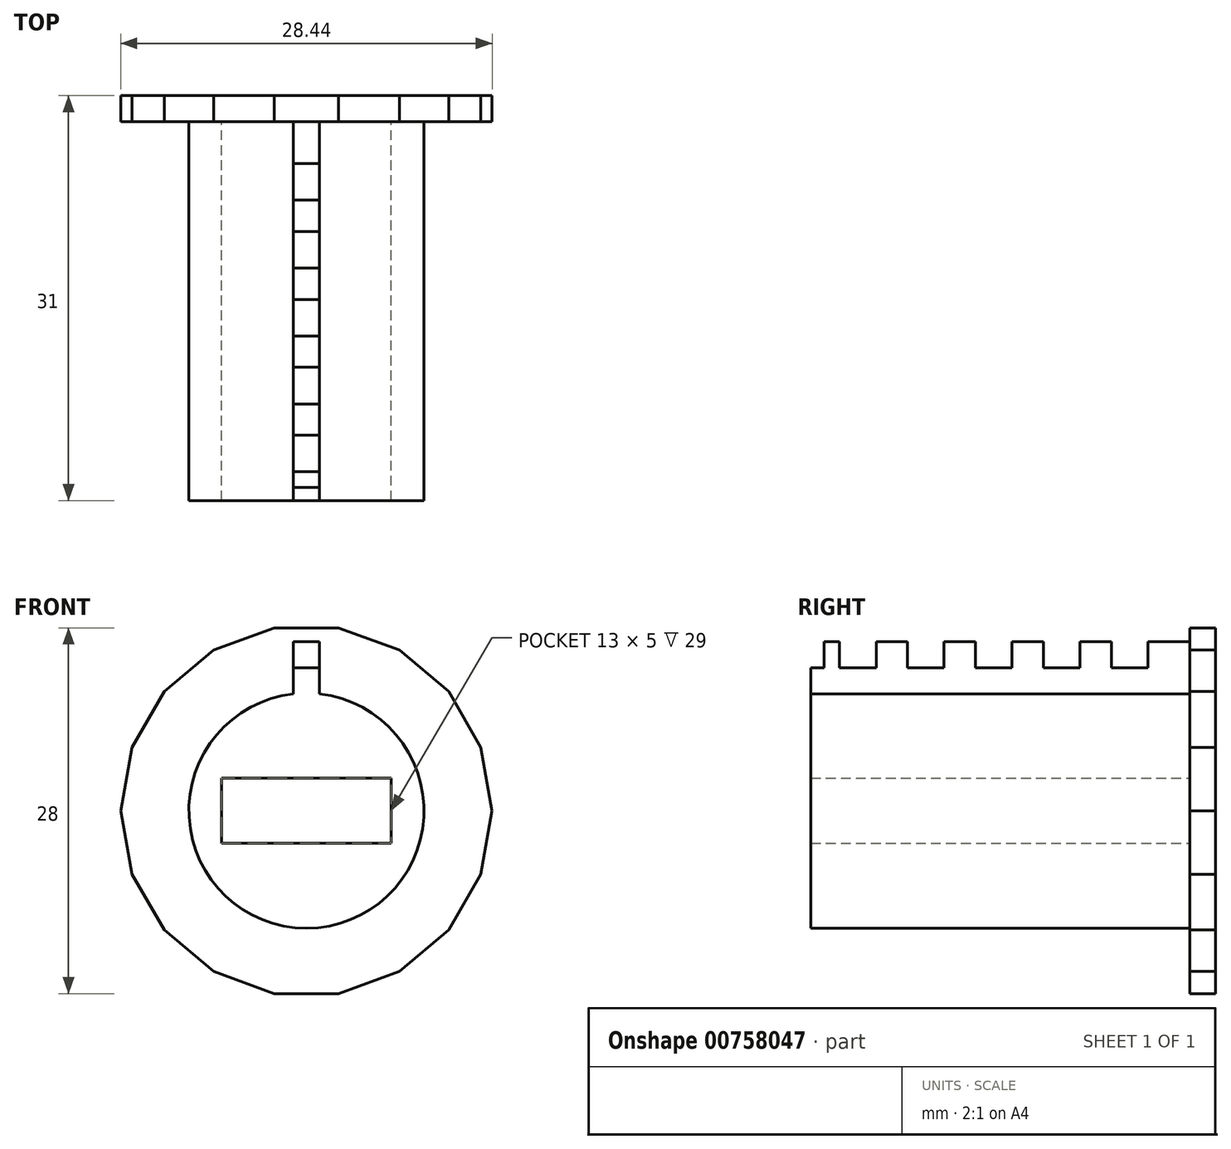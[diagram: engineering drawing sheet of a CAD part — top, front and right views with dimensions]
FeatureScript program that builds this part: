
annotation { "Feature Type Name" : "Feature", "Feature Type Description" : "" }
export const myFeature = defineFeature(function(context is Context, id is Id, definition is map)
    precondition{}
    {
        {
            var Q0;
            Q0=qCreatedBy(makeId("Front.planeOp"),FACE);
            var sketch = newSketch(context, id + "F0", { "sketchPlane" : qUnion([Q0])});
            skCircle(sketch, "E0", {"center": v(0, 0) * mm, "radius": 9 * mm});
            skCircle(sketch, "E1.cCircle", {"center": v(0, 0) * mm, "radius": 14 * mm, "construction": true});
            skLineSegment(sketch, "E1.0", {"start": v(-2.47, 14) * mm, "end": v(2.47, 14) * mm});
            skLineSegment(sketch, "E1.1", {"start": v(2.47, 14) * mm, "end": v(7.1, 12.31) * mm});
            skLineSegment(sketch, "E1.2", {"start": v(7.1, 12.31) * mm, "end": v(10.9, 9.14) * mm});
            skLineSegment(sketch, "E1.3", {"start": v(10.9, 9.14) * mm, "end": v(13.36, 4.86) * mm});
            skLineSegment(sketch, "E1.4", {"start": v(13.36, 4.86) * mm, "end": v(14.22, 0) * mm});
            skLineSegment(sketch, "E1.5", {"start": v(14.22, 0) * mm, "end": v(13.36, -4.86) * mm});
            skLineSegment(sketch, "E1.6", {"start": v(13.36, -4.86) * mm, "end": v(10.9, -9.14) * mm});
            skLineSegment(sketch, "E1.7", {"start": v(10.9, -9.14) * mm, "end": v(7.1, -12.31) * mm});
            skLineSegment(sketch, "E1.8", {"start": v(7.1, -12.31) * mm, "end": v(2.47, -14) * mm});
            skLineSegment(sketch, "E1.9", {"start": v(2.47, -14) * mm, "end": v(-2.47, -14) * mm});
            skLineSegment(sketch, "E1.10", {"start": v(-2.47, -14) * mm, "end": v(-7.1, -12.31) * mm});
            skLineSegment(sketch, "E1.11", {"start": v(-7.1, -12.31) * mm, "end": v(-10.9, -9.14) * mm});
            skLineSegment(sketch, "E1.12", {"start": v(-10.9, -9.14) * mm, "end": v(-13.36, -4.86) * mm});
            skLineSegment(sketch, "E1.13", {"start": v(-13.36, -4.86) * mm, "end": v(-14.22, 0) * mm});
            skLineSegment(sketch, "E1.14", {"start": v(-14.22, 0) * mm, "end": v(-13.36, 4.86) * mm});
            skLineSegment(sketch, "E1.15", {"start": v(-13.36, 4.86) * mm, "end": v(-10.9, 9.14) * mm});
            skLineSegment(sketch, "E1.16", {"start": v(-10.9, 9.14) * mm, "end": v(-7.1, 12.31) * mm});
            skLineSegment(sketch, "E1.17", {"start": v(-7.1, 12.31) * mm, "end": v(-2.47, 14) * mm});
            skPoint(sketch, "E1.0.midPoint", {"position": v(0, 14) * mm});
            skLineSegment(sketch, "E2.top", {"start": v(-1, 10.94) * mm, "end": v(1, 10.94) * mm});
            skLineSegment(sketch, "E2.left", {"start": v(-1, 8.94) * mm, "end": v(-1, 10.94) * mm});
            skLineSegment(sketch, "E2.right", {"start": v(1, 8.94) * mm, "end": v(1, 10.94) * mm});
            skLineSegment(sketch, "E3.bottom", {"start": v(7, 2.5) * mm, "end": v(-7, 2.5) * mm});
            skLineSegment(sketch, "E3.top", {"start": v(7, -2.5) * mm, "end": v(-7, -2.5) * mm});
            skLineSegment(sketch, "E3.left", {"start": v(7, 2.5) * mm, "end": v(7, -2.5) * mm});
            skLineSegment(sketch, "E3.right", {"start": v(-7, 2.5) * mm, "end": v(-7, -2.5) * mm});
            skSolve(sketch);
        }
        {
            var Q0;
            Q0 = qSketchRegion(id + "F0", true);
            var Q1;
            Q1=makeQuery(id+"F0.imprint","IMPRINT",FACE,{"disambiguationData":[TD([[makeQuery(id+"F0.imprint","IMPRINT",EDGE,{"derivedFrom":sQuery(id+"F0.wireOp",EDGE,"E2.top")}),-1.0]])]});
            var Q2;
            Q2=makeQuery(id+"F0.imprint","IMPRINT",FACE,{"disambiguationData":[TD([[makeQuery(id+"F0.imprint","IMPRINT",EDGE,{"derivedFrom":sQuery(id+"F0.wireOp",EDGE,"E3.bottom")}),-1.0]])]});
            var Q3;
            Q3=makeQuery(id+"F0.imprint","IMPRINT",FACE,{"disambiguationData":[TD([[makeQuery(id+"F0.imprint","IMPRINT",EDGE,{"derivedFrom":sQuery(id+"F0.wireOp",EDGE,"E3.bottom")}),1.0]])]});
            extrude(context, id + "F1", {"entities" : qUnion([Q0, Q1, Q2, Q3]), "depth" : 2 * mm, "offsetDistance" : 25 * mm});
        }
        {
            var Q0;
            Q0=qCreatedBy(makeId("Front.planeOp"),FACE);
            var sketch = newSketch(context, id + "F2", { "sketchPlane" : qUnion([Q0])});
            skLineSegment(sketch, "E4.bottom", {"start": v(6.5, 2.5) * mm, "end": v(-6.5, 2.5) * mm});
            skLineSegment(sketch, "E4.top", {"start": v(6.5, -2.5) * mm, "end": v(-6.5, -2.5) * mm});
            skLineSegment(sketch, "E4.left", {"start": v(6.5, 2.5) * mm, "end": v(6.5, -2.5) * mm});
            skLineSegment(sketch, "E4.right", {"start": v(-6.5, 2.5) * mm, "end": v(-6.5, -2.5) * mm});
            skPoint(sketch, "E4.middle", {"position": v(0, 0) * mm});
            skArc(sketch, "E5", {"start": v(-1, 8.94) * mm, "mid": v(0, -9) * mm, "end": v(1, 8.94) * mm});
            skLineSegment(sketch, "E6.top", {"start": v(-1, 10.94) * mm, "end": v(1, 10.94) * mm});
            skLineSegment(sketch, "E6.left", {"start": v(-1, 8.94) * mm, "end": v(-1, 10.94) * mm});
            skLineSegment(sketch, "E6.right", {"start": v(1, 8.94) * mm, "end": v(1, 10.94) * mm});
            skSolve(sketch);
        }
        {
            var Q0;
            Q0 = qSketchRegion(id + "F2", true);
            extrude(context, id + "F3", {"entities" : qUnion([Q0]), "operationType" : NewBodyOperationType.ADD, "depth" : 31 * mm, "offsetDistance" : 25 * mm});
        }
        {
            var Q0;
            Q0=makeQuery(id+"F3.opExtrude","SWEPT_FACE",FACE,{"disambiguationData":[OSD([sQuery(id+"F2.wireOp",EDGE,"E6.top")])]});
            var sketch = newSketch(context, id + "F4", { "sketchPlane" : qUnion([Q0])});
            skLineSegment(sketch, "E7.left", {"start": v(1, -2) * mm, "end": v(1, -4) * mm});
            skLineSegment(sketch, "E7.right", {"start": v(-1, -2) * mm, "end": v(-1, -4) * mm});
            skLineSegment(sketch, "E8.left", {"start": v(1, -4) * mm, "end": v(1, -9.2) * mm});
            skLineSegment(sketch, "E8.right", {"start": v(-1, -4) * mm, "end": v(-1, -9.2) * mm});
            skLineSegment(sketch, "E9.top", {"start": v(-1, -14.4) * mm, "end": v(1, -14.4) * mm});
            skLineSegment(sketch, "E9.left", {"start": v(-1, -9.2) * mm, "end": v(-1, -14.4) * mm});
            skLineSegment(sketch, "E9.right", {"start": v(1, -9.2) * mm, "end": v(1, -14.4) * mm});
            skLineSegment(sketch, "E10.top", {"start": v(-1, -19.6) * mm, "end": v(1, -19.6) * mm});
            skLineSegment(sketch, "E10.left", {"start": v(-1, -14.4) * mm, "end": v(-1, -19.6) * mm});
            skLineSegment(sketch, "E10.right", {"start": v(1, -14.4) * mm, "end": v(1, -19.6) * mm});
            skLineSegment(sketch, "E11.top", {"start": v(-1, -24.8) * mm, "end": v(1, -24.8) * mm});
            skLineSegment(sketch, "E11.left", {"start": v(-1, -19.6) * mm, "end": v(-1, -24.8) * mm});
            skLineSegment(sketch, "E11.right", {"start": v(1, -19.6) * mm, "end": v(1, -24.8) * mm});
            skLineSegment(sketch, "E12.top", {"start": v(-1, -30) * mm, "end": v(1, -30) * mm});
            skLineSegment(sketch, "E12.left", {"start": v(-1, -24.8) * mm, "end": v(-1, -30) * mm});
            skLineSegment(sketch, "E12.right", {"start": v(1, -24.8) * mm, "end": v(1, -30) * mm});
            skLineSegment(sketch, "E13", {"start": v(1, -5.2) * mm, "end": v(-1, -5.2) * mm});
            skLineSegment(sketch, "E14", {"start": v(1, -8) * mm, "end": v(-1, -8) * mm});
            skLineSegment(sketch, "E15", {"start": v(1, -10.4) * mm, "end": v(-1, -10.4) * mm});
            skLineSegment(sketch, "E16", {"start": v(1, -13.2) * mm, "end": v(-1, -13.2) * mm});
            skLineSegment(sketch, "E17", {"start": v(1, -15.6) * mm, "end": v(-1, -15.6) * mm});
            skLineSegment(sketch, "E18", {"start": v(1, -18.4) * mm, "end": v(-1, -18.4) * mm});
            skLineSegment(sketch, "E19", {"start": v(1, -20.8) * mm, "end": v(-1, -20.8) * mm});
            skLineSegment(sketch, "E20", {"start": v(1, -23.6) * mm, "end": v(-1, -23.6) * mm});
            skLineSegment(sketch, "E21", {"start": v(1, -26) * mm, "end": v(-1, -26) * mm});
            skLineSegment(sketch, "E22", {"start": v(1, -28.8) * mm, "end": v(-1, -28.8) * mm});
            skLineSegment(sketch, "E23", {"start": v(1, -2) * mm, "end": v(-1, -2) * mm});
            skSolve(sketch);
        }
        {
            var Q0;
            {var subQ4=sQuery(id+"F4.wireOp",EDGE,"E7.left");Q0=makeQuery(id+"F4.imprint","IMPRINT",FACE,{"disambiguationData":[TD([[makeQuery(id+"F4.imprint","IMPRINT",EDGE,{"derivedFrom":subQ4}),1.0]])]});}
            var Q1;
            {var subQ4=sQuery(id+"F4.wireOp",EDGE,"E14");Q1=makeQuery(id+"F4.imprint","IMPRINT",FACE,{"disambiguationData":[TD([[makeQuery(id+"F4.imprint","IMPRINT",EDGE,{"derivedFrom":subQ4}),1.0]])]});}
            var Q2;
            {var subQ0=sQuery(id+"F4.wireOp",EDGE,"E9.top");Q2=makeQuery(id+"F4.imprint","IMPRINT",FACE,{"disambiguationData":[TD([[makeQuery(id+"F4.imprint","IMPRINT",EDGE,{"derivedFrom":subQ0}),1.0]])]});}
            var Q3;
            {var subQ0=sQuery(id+"F4.wireOp",EDGE,"E9.top");Q3=makeQuery(id+"F4.imprint","IMPRINT",FACE,{"disambiguationData":[TD([[makeQuery(id+"F4.imprint","IMPRINT",EDGE,{"derivedFrom":subQ0}),-1.0]])]});}
            var Q4;
            {var subQ0=sQuery(id+"F4.wireOp",EDGE,"E10.top");Q4=makeQuery(id+"F4.imprint","IMPRINT",FACE,{"disambiguationData":[TD([[makeQuery(id+"F4.imprint","IMPRINT",EDGE,{"derivedFrom":subQ0}),1.0]])]});}
            var Q5;
            {var subQ0=sQuery(id+"F4.wireOp",EDGE,"E10.top");Q5=makeQuery(id+"F4.imprint","IMPRINT",FACE,{"disambiguationData":[TD([[makeQuery(id+"F4.imprint","IMPRINT",EDGE,{"derivedFrom":subQ0}),-1.0]])]});}
            var Q6;
            {var subQ0=sQuery(id+"F4.wireOp",EDGE,"E11.top");Q6=makeQuery(id+"F4.imprint","IMPRINT",FACE,{"disambiguationData":[TD([[makeQuery(id+"F4.imprint","IMPRINT",EDGE,{"derivedFrom":subQ0}),1.0]])]});}
            var Q7;
            {var subQ0=sQuery(id+"F4.wireOp",EDGE,"E11.top");Q7=makeQuery(id+"F4.imprint","IMPRINT",FACE,{"disambiguationData":[TD([[makeQuery(id+"F4.imprint","IMPRINT",EDGE,{"derivedFrom":subQ0}),-1.0]])]});}
            var Q8;
            {var subQ0=sQuery(id+"F4.wireOp",EDGE,"E12.top");Q8=makeQuery(id+"F4.imprint","IMPRINT",FACE,{"disambiguationData":[TD([[makeQuery(id+"F4.imprint","IMPRINT",EDGE,{"derivedFrom":subQ0}),1.0]])]});}
            extrude(context, id + "F5", {"entities" : qUnion([Q0, Q1, Q2, Q3, Q4, Q5, Q6, Q7, Q8]), "operationType" : NewBodyOperationType.ADD, "depth" : 2 * mm, "offsetDistance" : 25 * mm});
        }
    });
